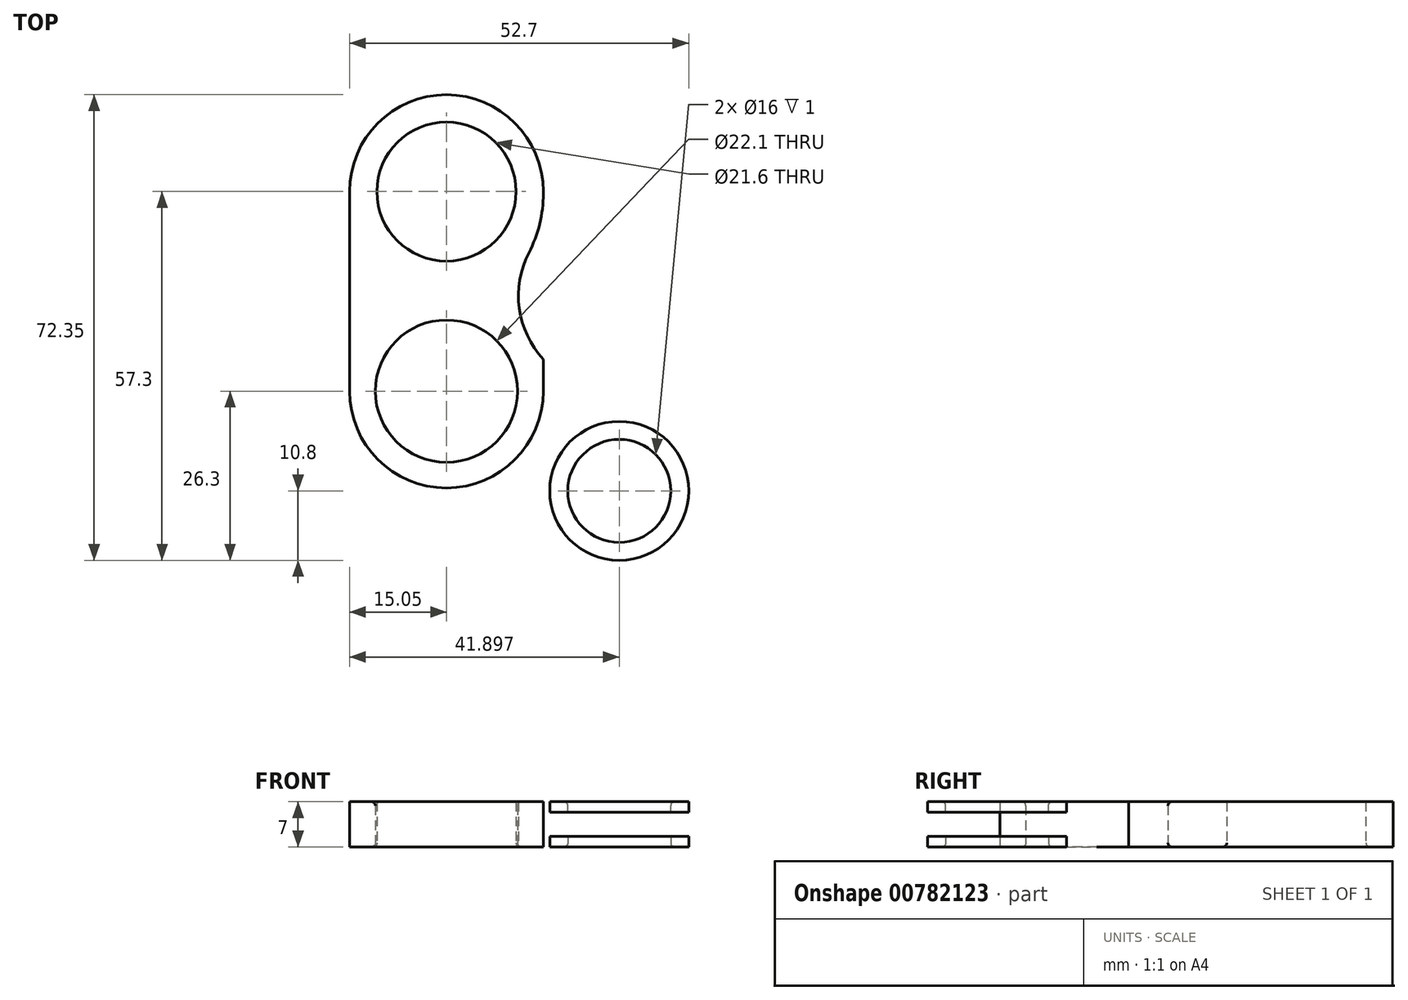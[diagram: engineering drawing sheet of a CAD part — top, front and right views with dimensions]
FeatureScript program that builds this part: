
annotation { "Feature Type Name" : "Feature", "Feature Type Description" : "" }
export const myFeature = defineFeature(function(context is Context, id is Id, definition is map)
    precondition{}
    {
        {
            var Q0;
            Q0=qCreatedBy(makeId("Top.planeOp"),FACE);
            var sketch = newSketch(context, id + "F0", { "sketchPlane" : qUnion([Q0])});
            skCircle(sketch, "E0", {"center": v(0, 0) * mm, "radius": 11.05 * mm});
            skCircle(sketch, "E1", {"center": v(0, 0) * mm, "radius": 15.05 * mm});
            skSolve(sketch);
        }
        {
            var Q0;
            Q0=qSketchRegion(id+"F0",true);
            extrude(context, id + "F1", {"entities" : qUnion([Q0]), "depth" : 7 * mm, "offsetDistance" : 25 * mm});
        }
        {
            var Q0;
            Q0=qCreatedBy(makeId("Top.planeOp"),FACE);
            var sketch = newSketch(context, id + "F2", { "sketchPlane" : qUnion([Q0])});
            skCircle(sketch, "E2", {"center": v(0, 31) * mm, "radius": 10.8 * mm});
            skArc(sketch, "E3", {"start": v(15.05, 31) * mm, "mid": v(0, 46.05) * mm, "end": v(-15.05, 31) * mm});
            skArc(sketch, "E4.0", {"start": v(15.05, 0) * mm, "mid": v(0, 15.05) * mm, "end": v(-15.05, 0) * mm});
            skLineSegment(sketch, "E5", {"start": v(0, 31) * mm, "end": v(-15.05, 31) * mm, "construction": true});
            skLineSegment(sketch, "E6", {"start": v(0, 31) * mm, "end": v(15.05, 31) * mm, "construction": true});
            skLineSegment(sketch, "E7", {"start": v(0, 0) * mm, "end": v(-15.05, 0) * mm, "construction": true});
            skLineSegment(sketch, "E8", {"start": v(0, 0) * mm, "end": v(15.05, 0) * mm, "construction": true});
            skLineSegment(sketch, "E9", {"start": v(-15.05, 31) * mm, "end": v(-15.05, 0) * mm});
            skLineSegment(sketch, "E10", {"start": v(15.05, 31) * mm, "end": v(15.05, 0) * mm});
            skSolve(sketch);
        }
        {
            var Q0;
            Q0=qSketchRegion(id+"F2",true);
            var Q1;
            Q1=makeQuery(id+"F1.opExtrude","CAP_FACE",FACE,{"disambiguationData":[OSD([sQuery(id+"F0.wireOp",EDGE,"E0"),sQuery(id+"F0.wireOp",EDGE,"E1")])],"isStart":false});
            extrude(context, id + "F3", {"entities" : qUnion([Q0]), "operationType" : NewBodyOperationType.ADD, "endBound" : BoundingType.UP_TO_SURFACE, "depth" : 25 * mm, "endBoundEntityFace" : qUnion([Q1]), "offsetDistance" : 25 * mm});
        }
        {
            var Q0;
            Q0=qCreatedBy(makeId("Top.planeOp"),FACE);
            var sketch = newSketch(context, id + "F4", { "sketchPlane" : qUnion([Q0])});
            skLineSegment(sketch, "E11.0", {"start": v(15.05, 24.69) * mm, "end": v(15.05, 8.69) * mm});
            skLineSegment(sketch, "E12.0", {"start": v(28.9, 0.69) * mm, "end": v(15.05, 8.69) * mm});
            skArc(sketch, "E13", {"start": v(15.05, 24.69) * mm, "mid": v(13.12, 7.58) * mm, "end": v(28.9, 0.69) * mm});
            skPoint(sketch, "E14.orphan", {"position": v(15.05, 31) * mm});
            skPoint(sketch, "E15.orphan", {"position": v(34.37, -2.47) * mm});
            skSolve(sketch);
        }
        {
            var Q0;
            Q0=qSketchRegion(id+"F4",true);
            var Q1;
            {var subQ0=sQuery(id+"F2.wireOp",EDGE,"E10");var subQ1=sQuery(id+"F2.wireOp",EDGE,"E9");var subQ2=sQuery(id+"F2.wireOp",EDGE,"E4.0");var subQ3=sQuery(id+"F2.wireOp",EDGE,"E3");var subQ4=sQuery(id+"F2.wireOp",EDGE,"E2");Q1=makeQuery(id+"F0EbBsUhQH7FECo_1.2.F3.boolean.opBoolean","MERGE",FACE,{"derivedFrom":[makeQuery(id+"F0EbBsUhQH7FECo_1.1.F3.boolean.opBoolean","MERGE",FACE,{"derivedFrom":[makeQuery(id+"F3.boolean.opBoolean","MERGE",FACE,{"derivedFrom":[makeQuery(id+"F1.opExtrude","CAP_FACE",FACE,{"disambiguationData":[OSD([sQuery(id+"F0.wireOp",EDGE,"E0"),sQuery(id+"F0.wireOp",EDGE,"E1")])],"isStart":false}),makeQuery(id+"F3.opExtrude","CAP_FACE",FACE,{"disambiguationData":[OSD([subQ4,subQ3,subQ2,subQ1,subQ0])],"isStart":false})]}),makeQuery(id+"F0EbBsUhQH7FECo_1.1.F3.opExtrude","CAP_FACE",FACE,{"disambiguationData":[OSD([subQ4,subQ3,subQ2,subQ1,subQ0])],"isStart":false})]}),makeQuery(id+"F0EbBsUhQH7FECo_1.2.F3.opExtrude","CAP_FACE",FACE,{"disambiguationData":[OSD([subQ4,subQ3,subQ2,subQ1,subQ0])],"isStart":false})]});}
            extrude(context, id + "F5", {"entities" : qUnion([Q0]), "operationType" : NewBodyOperationType.REMOVE, "endBound" : BoundingType.UP_TO_SURFACE, "depth" : 25 * mm, "endBoundEntityFace" : qUnion([Q1]), "offsetDistance" : 25 * mm});
        }
        {
            var Q0;
            Q0=makeQuery(id+"F5.boolean.opBoolean","COPY",EDGE,{"derivedFrom":makeQuery(id+"F5.opExtrude","SWEPT_EDGE",EDGE,{"disambiguationData":[OSD([sQuery(id+"F4.wireOp",EDGE,"E11.0"),sQuery(id+"F4.wireOp",EDGE,"E13")])]})});
            var Q1;
            Q1=makeQuery(id+"FjNaIixI5rsmLLj_1.1.F5.boolean.opBoolean","COPY",EDGE,{"derivedFrom":makeQuery(id+"FjNaIixI5rsmLLj_1.1.F5.opExtrude","SWEPT_EDGE",EDGE,{"disambiguationData":[OSD([sQuery(id+"F4.wireOp",EDGE,"E12.0"),sQuery(id+"F4.wireOp",EDGE,"E13")])]})});
            var Q2;
            Q2=makeQuery(id+"F5.boolean.opBoolean","COPY",EDGE,{"derivedFrom":makeQuery(id+"F5.opExtrude","SWEPT_EDGE",EDGE,{"disambiguationData":[OSD([sQuery(id+"F4.wireOp",EDGE,"E12.0"),sQuery(id+"F4.wireOp",EDGE,"E13")])]})});
            var Q3;
            Q3=makeQuery(id+"FjNaIixI5rsmLLj_1.1.F5.boolean.opBoolean","COPY",EDGE,{"derivedFrom":makeQuery(id+"FjNaIixI5rsmLLj_1.1.F5.opExtrude","SWEPT_EDGE",EDGE,{"disambiguationData":[OSD([sQuery(id+"F4.wireOp",EDGE,"E11.0"),sQuery(id+"F4.wireOp",EDGE,"E13")])]})});
            var Q4;
            Q4=makeQuery(id+"FjNaIixI5rsmLLj_1.2.F5.boolean.opBoolean","COPY",EDGE,{"derivedFrom":makeQuery(id+"FjNaIixI5rsmLLj_1.2.F5.opExtrude","SWEPT_EDGE",EDGE,{"disambiguationData":[OSD([sQuery(id+"F4.wireOp",EDGE,"E12.0"),sQuery(id+"F4.wireOp",EDGE,"E13")])]})});
            var Q5;
            Q5=makeQuery(id+"FjNaIixI5rsmLLj_1.2.F5.boolean.opBoolean","COPY",EDGE,{"derivedFrom":makeQuery(id+"FjNaIixI5rsmLLj_1.2.F5.opExtrude","SWEPT_EDGE",EDGE,{"disambiguationData":[OSD([sQuery(id+"F4.wireOp",EDGE,"E11.0"),sQuery(id+"F4.wireOp",EDGE,"E13")])]})});
            fillet(context, id + "F6", {"entities" : qUnion([Q0, Q1, Q2, Q3, Q4, Q5]), "radius" : 20 * mm, "tangentPropagation" : true, "allowEdgeOverflow" : false});
        }
        {
            var Q0;
            Q0=qCreatedBy(makeId("Top.planeOp"),FACE);
            var sketch = newSketch(context, id + "F7", { "sketchPlane" : qUnion([Q0])});
            skCircle(sketch, "E16.0", {"center": v(26.85, -15.5) * mm, "radius": 10.8 * mm});
            skCircle(sketch, "E17", {"center": v(26.85, -15.5) * mm, "radius": 8 * mm});
            skSolve(sketch);
        }
        {
            var Q0;
            Q0 = qSketchRegion(id + "F7", true);
            extrude(context, id + "F8", {"entities" : qUnion([Q0]), "operationType" : NewBodyOperationType.ADD, "depth" : 1.6 * mm, "offsetDistance" : 25 * mm});
        }
        {
            var Q0;
            {var subQ0=sQuery(id+"F2.wireOp",EDGE,"E10");var subQ1=sQuery(id+"F2.wireOp",EDGE,"E9");var subQ2=sQuery(id+"F2.wireOp",EDGE,"E4.0");var subQ3=sQuery(id+"F2.wireOp",EDGE,"E3");var subQ4=sQuery(id+"F2.wireOp",EDGE,"E2");Q0=makeQuery(id+"F0EbBsUhQH7FECo_1.2.F3.boolean.opBoolean","MERGE",FACE,{"derivedFrom":[makeQuery(id+"F0EbBsUhQH7FECo_1.1.F3.boolean.opBoolean","MERGE",FACE,{"derivedFrom":[makeQuery(id+"F3.boolean.opBoolean","MERGE",FACE,{"derivedFrom":[makeQuery(id+"F1.opExtrude","CAP_FACE",FACE,{"disambiguationData":[OSD([sQuery(id+"F0.wireOp",EDGE,"E0"),sQuery(id+"F0.wireOp",EDGE,"E1")])],"isStart":false}),makeQuery(id+"F3.opExtrude","CAP_FACE",FACE,{"disambiguationData":[OSD([subQ4,subQ3,subQ2,subQ1,subQ0])],"isStart":false})]}),makeQuery(id+"F0EbBsUhQH7FECo_1.1.F3.opExtrude","CAP_FACE",FACE,{"disambiguationData":[OSD([subQ4,subQ3,subQ2,subQ1,subQ0])],"isStart":false})]}),makeQuery(id+"F0EbBsUhQH7FECo_1.2.F3.opExtrude","CAP_FACE",FACE,{"disambiguationData":[OSD([subQ4,subQ3,subQ2,subQ1,subQ0])],"isStart":false})]});}
            var sketch = newSketch(context, id + "F9", { "sketchPlane" : qUnion([Q0])});
            skCircle(sketch, "E18.0", {"center": v(26.85, -15.5) * mm, "radius": 10.8 * mm});
            skCircle(sketch, "E19.0", {"center": v(26.85, -15.5) * mm, "radius": 8 * mm});
            skSolve(sketch);
        }
        {
            var Q0;
            Q0 = qSketchRegion(id + "F9", true);
            extrude(context, id + "F10", {"entities" : qUnion([Q0]), "operationType" : NewBodyOperationType.ADD, "oppositeDirection" : true, "depth" : 1.6 * mm, "offsetDistance" : 25 * mm});
        }
        {
            var Q0;
            Q0=makeQuery(id+"F0EbBsUhQH7FECo_1.1.F3.opExtrude","CAP_EDGE",EDGE,{"disambiguationData":[OSD([sQuery(id+"F2.wireOp",EDGE,"E9")])],"isStart":false});
            var Q1;
            Q1=makeQuery(id+"F0EbBsUhQH7FECo_1.1.F3.opExtrude","CAP_EDGE",EDGE,{"disambiguationData":[OSD([sQuery(id+"F2.wireOp",EDGE,"E9")])],"isStart":true});
            var Q2;
            Q2=makeQuery(id+"F3.opExtrude","TWEAK_EDGE",EDGE,{"derivedFrom":[makeQuery(id+"F1.opExtrude","CAP_FACE",FACE,{"disambiguationData":[OSD([sQuery(id+"F0.wireOp",EDGE,"E0"),sQuery(id+"F0.wireOp",EDGE,"E1")])],"isStart":false}),makeQuery(id+"F2.imprint","IMPRINT",EDGE,{"derivedFrom":sQuery(id+"F2.wireOp",EDGE,"E2")})]});
            var Q3;
            Q3=makeQuery(id+"F1.opExtrude","CAP_EDGE",EDGE,{"disambiguationData":[OSD([sQuery(id+"F0.wireOp",EDGE,"E0")])],"isStart":false});
            var Q4;
            {var subQ0=sQuery(id+"F0.wireOp",EDGE,"E1");var subQ1=sQuery(id+"F0.wireOp",EDGE,"E0");Q4=makeQuery(id+"F0EbBsUhQH7FECo_1.1.F3.opExtrude","TWEAK_EDGE",EDGE,{"derivedFrom":[makeQuery(id+"F2.imprint","IMPRINT",EDGE,{"derivedFrom":sQuery(id+"F2.wireOp",EDGE,"E2")}),makeQuery(id+"F3.boolean.opBoolean","MERGE",FACE,{"derivedFrom":[makeQuery(id+"F1.opExtrude","CAP_FACE",FACE,{"disambiguationData":[OSD([subQ1,subQ0])],"isStart":false}),makeQuery(id+"F3.opExtrude","CAP_FACE",FACE,{"disambiguationData":[OSD([subQ1,subQ0])],"isStart":false})]})]});}
            var Q5;
            {var subQ0=sQuery(id+"F0.wireOp",EDGE,"E1");var subQ1=sQuery(id+"F0.wireOp",EDGE,"E0");Q5=makeQuery(id+"F0EbBsUhQH7FECo_1.2.F3.opExtrude","TWEAK_EDGE",EDGE,{"derivedFrom":[makeQuery(id+"F2.imprint","IMPRINT",EDGE,{"derivedFrom":sQuery(id+"F2.wireOp",EDGE,"E2")}),makeQuery(id+"F0EbBsUhQH7FECo_1.1.F3.boolean.opBoolean","MERGE",FACE,{"derivedFrom":[makeQuery(id+"F3.boolean.opBoolean","MERGE",FACE,{"derivedFrom":[makeQuery(id+"F1.opExtrude","CAP_FACE",FACE,{"disambiguationData":[OSD([subQ1,subQ0])],"isStart":false}),makeQuery(id+"F3.opExtrude","CAP_FACE",FACE,{"disambiguationData":[OSD([subQ1,subQ0])],"isStart":false})]}),makeQuery(id+"F0EbBsUhQH7FECo_1.1.F3.opExtrude","CAP_FACE",FACE,{"disambiguationData":[OSD([subQ1,subQ0])],"isStart":false})]})]});}
            var Q6;
            Q6=makeQuery(id+"F0EbBsUhQH7FECo_1.1.F3.opExtrude","CAP_EDGE",EDGE,{"disambiguationData":[OSD([sQuery(id+"F2.wireOp",EDGE,"E2")])],"isStart":true});
            var Q7;
            Q7=makeQuery(id+"F1.opExtrude","CAP_EDGE",EDGE,{"disambiguationData":[OSD([sQuery(id+"F0.wireOp",EDGE,"E0")])],"isStart":true});
            var Q8;
            Q8=makeQuery(id+"F0EbBsUhQH7FECo_1.2.F3.opExtrude","CAP_EDGE",EDGE,{"disambiguationData":[OSD([sQuery(id+"F2.wireOp",EDGE,"E2")])],"isStart":true});
            var Q9;
            Q9=makeQuery(id+"F3.opExtrude","CAP_EDGE",EDGE,{"disambiguationData":[OSD([sQuery(id+"F2.wireOp",EDGE,"E2")])],"isStart":true});
            fillet(context, id + "F11", {"entities" : qUnion([Q0, Q1, Q2, Q3, Q4, Q5, Q6, Q7, Q8, Q9]), "radius" : .6 * mm, "tangentPropagation" : true, "allowEdgeOverflow" : false});
        }
        {
            var Q0;
            Q0=makeQuery(id+"FixblimBjk7ZGzs_1.1.F10.opExtrude","CAP_EDGE",EDGE,{"disambiguationData":[OSD([sQuery(id+"F9.wireOp",EDGE,"E19.0")])],"isStart":true});
            var Q1;
            Q1=makeQuery(id+"FixblimBjk7ZGzs_1.2.F10.opExtrude","CAP_EDGE",EDGE,{"disambiguationData":[OSD([sQuery(id+"F9.wireOp",EDGE,"E19.0")])],"isStart":true});
            var Q2;
            Q2=makeQuery(id+"F10.opExtrude","CAP_EDGE",EDGE,{"disambiguationData":[OSD([sQuery(id+"F9.wireOp",EDGE,"E19.0")])],"isStart":true});
            var Q3;
            Q3=makeQuery(id+"F8.opExtrude","CAP_EDGE",EDGE,{"disambiguationData":[OSD([sQuery(id+"F7.wireOp",EDGE,"E17")])],"isStart":true});
            var Q4;
            Q4=makeQuery(id+"FixblimBjk7ZGzs_1.1.F8.opExtrude","CAP_EDGE",EDGE,{"disambiguationData":[OSD([sQuery(id+"F7.wireOp",EDGE,"E17")])],"isStart":true});
            var Q5;
            Q5=makeQuery(id+"FixblimBjk7ZGzs_1.2.F8.opExtrude","CAP_EDGE",EDGE,{"disambiguationData":[OSD([sQuery(id+"F7.wireOp",EDGE,"E17")])],"isStart":true});
            fillet(context, id + "F12", {"entities" : qUnion([Q0, Q1, Q2, Q3, Q4, Q5]), "radius" : .6 * mm, "tangentPropagation" : true, "allowEdgeOverflow" : false});
        }
    });
